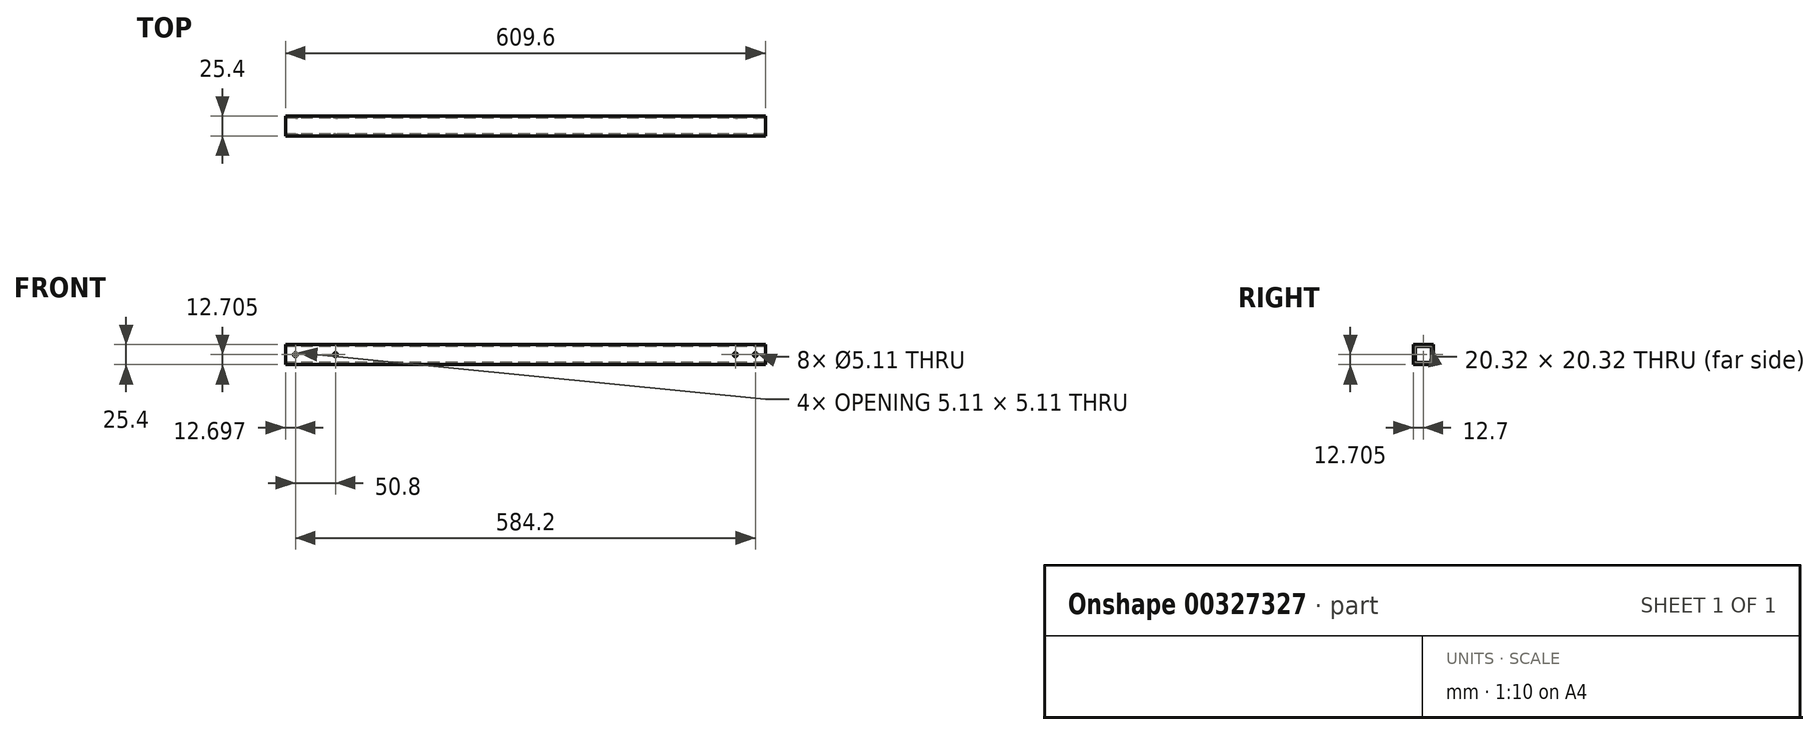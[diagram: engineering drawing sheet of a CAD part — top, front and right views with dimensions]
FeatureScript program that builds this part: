
annotation { "Feature Type Name" : "Feature", "Feature Type Description" : "" }
export const myFeature = defineFeature(function(context is Context, id is Id, definition is map)
    precondition{}
    {
        {
            var Q0;
            Q0=qCreatedBy(makeId("Front.planeOp"),FACE);
            var sketch = newSketch(context, id + "F0", { "sketchPlane" : qUnion([Q0])});
            skLineSegment(sketch, "E0.bottom", {"start": v(-95.08, 43.64) * mm, "end": v(514.52, 43.64) * mm});
            skLineSegment(sketch, "E0.top", {"start": v(-95.08, 18.24) * mm, "end": v(514.52, 18.24) * mm});
            skLineSegment(sketch, "E0.left", {"start": v(-95.08, 43.64) * mm, "end": v(-95.08, 18.24) * mm});
            skLineSegment(sketch, "E0.right", {"start": v(514.52, 43.64) * mm, "end": v(514.52, 18.24) * mm});
            skSolve(sketch);
        }
        {
            var Q0;
            Q0=makeQuery(id+"F0.imprint","IMPRINT",FACE,{"disambiguationData":[TD([[makeQuery(id+"F0.imprint","IMPRINT",EDGE,{"derivedFrom":sQuery(id+"F0.wireOp",EDGE,"E0.bottom")}),-1.0]])]});
            extrude(context, id + "F1", {"entities" : qUnion([Q0]), "depth" : 25.4 * mm});
        }
        {
            var Q0;
            Q0=makeQuery(id+"F1.opExtrude","SWEPT_FACE",FACE,{"disambiguationData":[OSD([sQuery(id+"F0.wireOp",EDGE,"E0.left")])]});
            var sketch = newSketch(context, id + "F2", { "sketchPlane" : qUnion([Q0])});
            skLineSegment(sketch, "E1.bottom", {"start": v(2.54, 41.1) * mm, "end": v(22.86, 41.1) * mm});
            skLineSegment(sketch, "E1.top", {"start": v(2.54, 20.78) * mm, "end": v(22.86, 20.78) * mm});
            skLineSegment(sketch, "E1.left", {"start": v(2.54, 41.1) * mm, "end": v(2.54, 20.78) * mm});
            skLineSegment(sketch, "E1.right", {"start": v(22.86, 41.1) * mm, "end": v(22.86, 20.78) * mm});
            skSolve(sketch);
        }
        {
            var Q0;
            Q0=makeQuery(id+"F2.imprint","IMPRINT",FACE,{"disambiguationData":[TD([[makeQuery(id+"F2.imprint","IMPRINT",EDGE,{"derivedFrom":sQuery(id+"F2.wireOp",EDGE,"E1.bottom")}),-1.0]])]});
            extrude(context, id + "F3", {"entities" : qUnion([Q0]), "operationType" : NewBodyOperationType.REMOVE, "oppositeDirection" : true, "depth" : 609.6 * mm});
        }
        {
            var Q0;
            Q0=makeQuery(id+"F1.opExtrude","CAP_FACE",FACE,{"disambiguationData":[OSD([sQuery(id+"F0.wireOp",EDGE,"E0.bottom"),sQuery(id+"F0.wireOp",EDGE,"E0.top"),sQuery(id+"F0.wireOp",EDGE,"E0.left"),sQuery(id+"F0.wireOp",EDGE,"E0.right")])],"isStart":false});
            var sketch = newSketch(context, id + "F4", { "sketchPlane" : qUnion([Q0])});
            skCircle(sketch, "E2", {"center": v(-82.38, 30.94) * mm, "radius": 2.55 * mm});
            skPoint(sketch, "E2.centerSnap0", {"position": v(-95.08, 30.94) * mm});
            skCircle(sketch, "E3", {"center": v(-31.58, 30.94) * mm, "radius": 2.55 * mm});
            skCircle(sketch, "E4", {"center": v(476.42, 30.94) * mm, "radius": 2.55 * mm});
            skCircle(sketch, "E5", {"center": v(501.82, 30.94) * mm, "radius": 2.55 * mm});
            skSolve(sketch);
        }
        {
            var Q0;
            Q0=makeQuery(id+"F4.imprint","IMPRINT",FACE,{"disambiguationData":[TD([[makeQuery(id+"F4.imprint","IMPRINT",EDGE,{"derivedFrom":sQuery(id+"F4.wireOp",EDGE,"E5")}),1.0]])]});
            var Q1;
            Q1=makeQuery(id+"F4.imprint","IMPRINT",FACE,{"disambiguationData":[TD([[makeQuery(id+"F4.imprint","IMPRINT",EDGE,{"derivedFrom":sQuery(id+"F4.wireOp",EDGE,"E4")}),1.0]])]});
            var Q2;
            Q2=makeQuery(id+"F4.imprint","IMPRINT",FACE,{"disambiguationData":[TD([[makeQuery(id+"F4.imprint","IMPRINT",EDGE,{"derivedFrom":sQuery(id+"F4.wireOp",EDGE,"E2")}),1.0]])]});
            var Q3;
            Q3=makeQuery(id+"F4.imprint","IMPRINT",FACE,{"disambiguationData":[TD([[makeQuery(id+"F4.imprint","IMPRINT",EDGE,{"derivedFrom":sQuery(id+"F4.wireOp",EDGE,"E3")}),1.0]])]});
            extrude(context, id + "F5", {"entities" : qUnion([Q0, Q1, Q2, Q3]), "operationType" : NewBodyOperationType.REMOVE, "oppositeDirection" : true, "depth" : 25.4 * mm});
        }
    });
